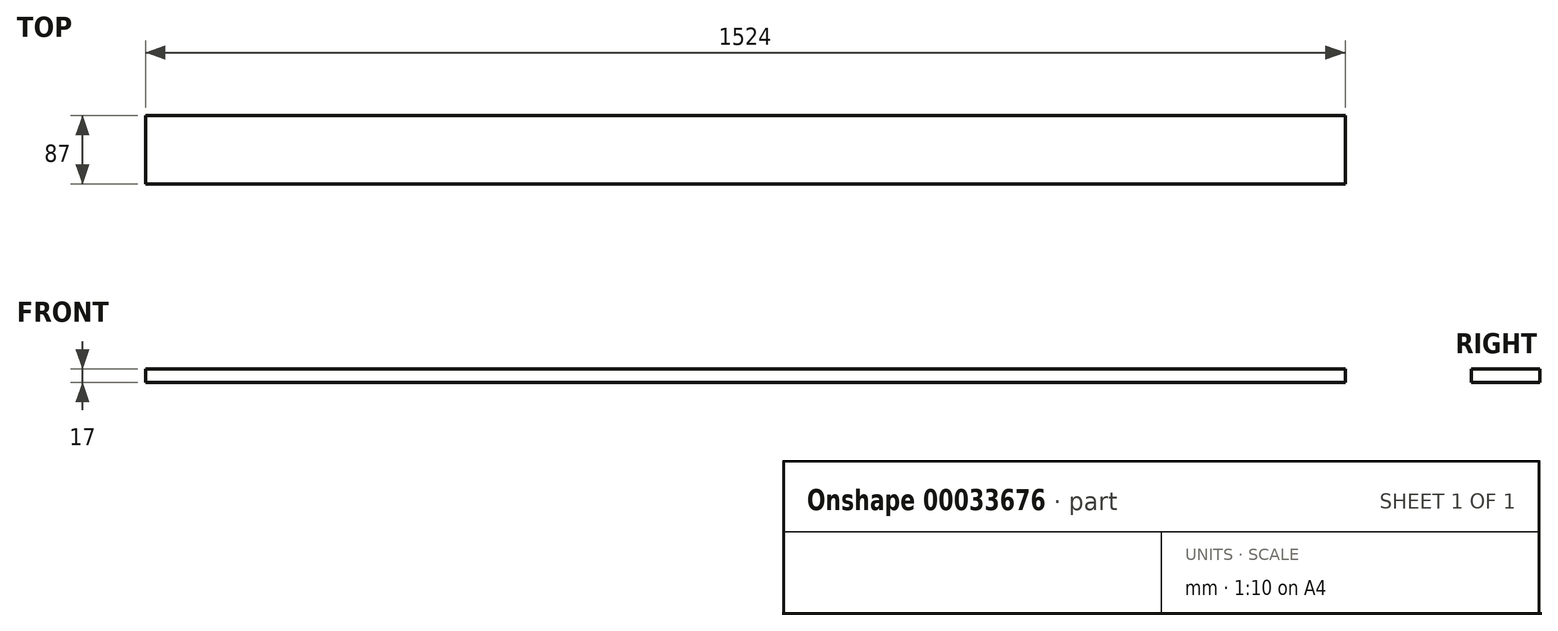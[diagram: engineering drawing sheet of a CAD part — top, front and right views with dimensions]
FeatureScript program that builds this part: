
annotation { "Feature Type Name" : "Feature", "Feature Type Description" : "" }
export const myFeature = defineFeature(function(context is Context, id is Id, definition is map)
    precondition{}
    {
        {
            var Q0;
            Q0=qCreatedBy(makeId("Right.planeOp"),FACE);
            var sketch = newSketch(context, id + "F0", { "sketchPlane" : qUnion([Q0])});
            skLineSegment(sketch, "E0.bottom", {"start": v(0, 0) * mm, "end": v(-87, 0) * mm});
            skLineSegment(sketch, "E0.top", {"start": v(0, 17) * mm, "end": v(-87, 17) * mm});
            skLineSegment(sketch, "E0.left", {"start": v(0, 0) * mm, "end": v(0, 17) * mm});
            skLineSegment(sketch, "E0.right", {"start": v(-87, 0) * mm, "end": v(-87, 17) * mm});
            skSolve(sketch);
        }
        {
            var Q0;
            Q0 = qSketchRegion(id + "F0", true);
            extrude(context, id + "F1", {"entities" : qUnion([Q0]), "depth" : 1524 * mm});
        }
    });
